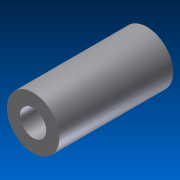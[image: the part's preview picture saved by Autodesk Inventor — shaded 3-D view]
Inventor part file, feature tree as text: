
AUTODESK INVENTOR PART (.ipt)
format: ipt  version: 2012 (Build 160160000, 160)  size: 81,408 bytes
history: native  units: in
note: dims shown in document units (in); Inventor stores cm internally (conversion verified against a paired STEP export)
features: extrude x1, sketch x1
ambient origin geometry x8: Origin, YZ Plane, XZ Plane, XY Plane, X Axis, Y Axis, Z Axis, Center Point
bodies: Solid1 (feature_tree)
feature tree (2):
  extrude  "Extrusion1"  Depth=0.2362in
  sketch  "Sketch1"  dims[d0=0.1181in d1=0.2362in d2=0.5118in d3=0.0in]
